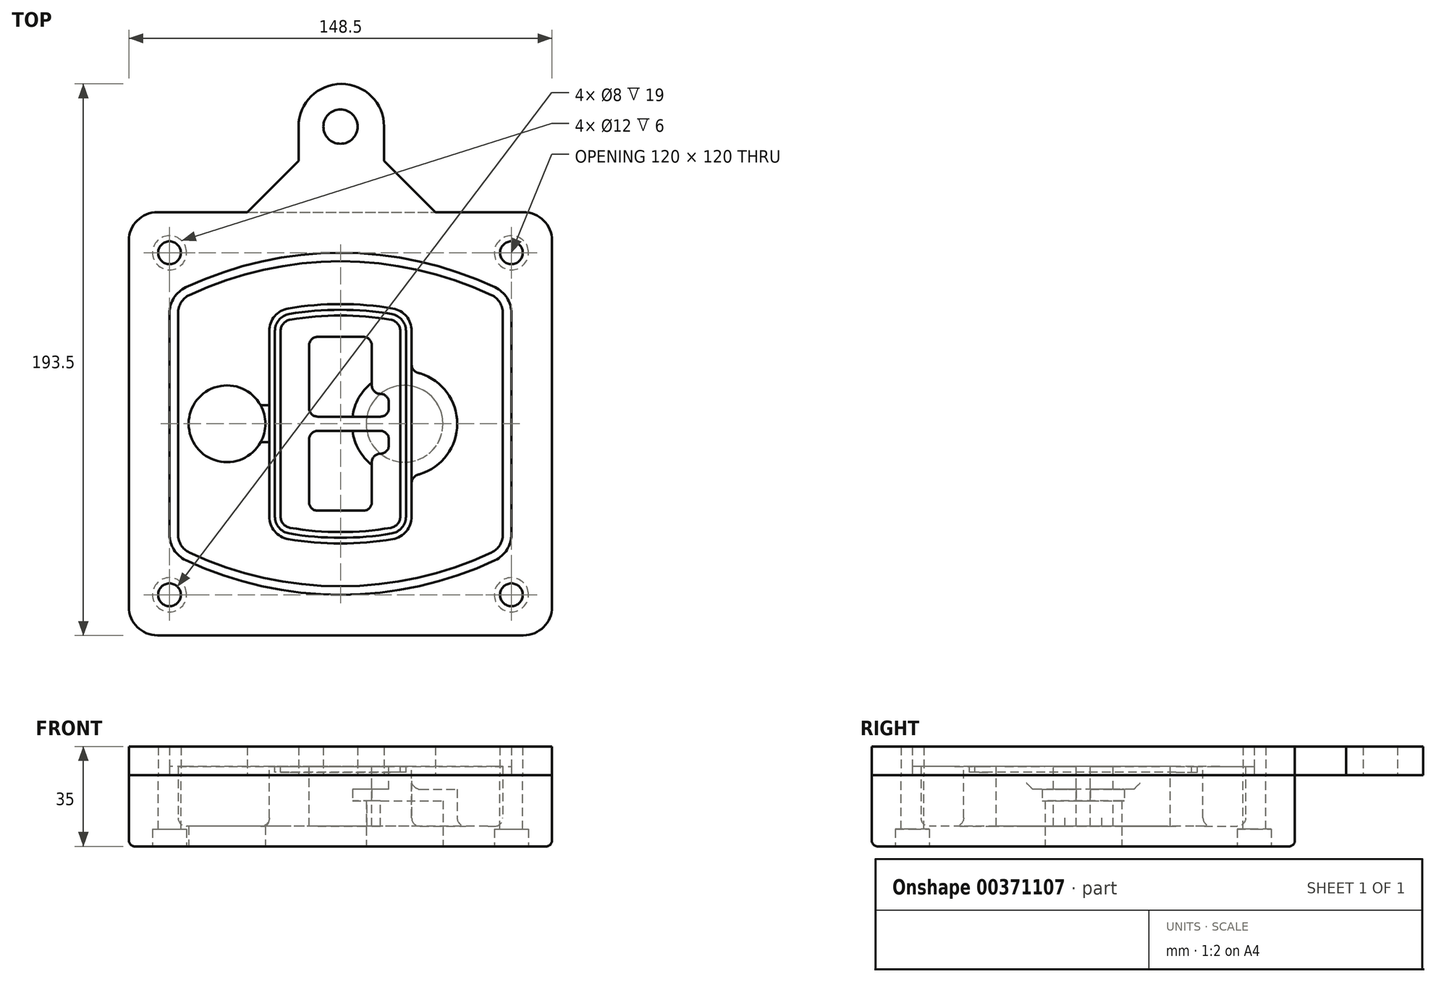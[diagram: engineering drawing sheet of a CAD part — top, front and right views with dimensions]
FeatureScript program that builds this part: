
annotation { "Feature Type Name" : "Feature", "Feature Type Description" : "" }
export const myFeature = defineFeature(function(context is Context, id is Id, definition is map)
    precondition{}
    {
        {
            var Q0;
            Q0=qCreatedBy(makeId("Top.planeOp"),FACE);
            var sketch = newSketch(context, id + "F0", { "sketchPlane" : qUnion([Q0])});
            skPoint(sketch, "E0.rect.middle", {"position": v(0, 0) * mm});
            skLineSegment(sketch, "E1.bottom", {"start": v(-64.25, -74.25) * mm, "end": v(64.25, -74.25) * mm});
            skLineSegment(sketch, "E1.top", {"start": v(-64.25, 74.25) * mm, "end": v(64.25, 74.25) * mm});
            skLineSegment(sketch, "E1.left", {"start": v(-74.25, -64.25) * mm, "end": v(-74.25, 64.25) * mm});
            skLineSegment(sketch, "E1.right", {"start": v(74.25, -64.25) * mm, "end": v(74.25, 64.25) * mm});
            skLineSegment(sketch, "E2", {"start": v(-74.25, 74.25) * mm, "end": v(74.25, -74.25) * mm, "construction": true});
            skLineSegment(sketch, "E3", {"start": v(74.25, 74.25) * mm, "end": v(-74.25, -74.25) * mm, "construction": true});
            skCircle(sketch, "E4", {"center": v(-60, 60) * mm, "radius": 4 * mm});
            skCircle(sketch, "E5", {"center": v(60, 60) * mm, "radius": 4 * mm});
            skCircle(sketch, "E6", {"center": v(60, -60) * mm, "radius": 4 * mm});
            skCircle(sketch, "E7", {"center": v(-60, -60) * mm, "radius": 4 * mm});
            skLineSegment(sketch, "E8", {"start": v(-60, 60) * mm, "end": v(60, 60) * mm, "construction": true});
            skLineSegment(sketch, "E9", {"start": v(60, 60) * mm, "end": v(60, -60) * mm, "construction": true});
            skLineSegment(sketch, "E10", {"start": v(60, -60) * mm, "end": v(-60, -60) * mm, "construction": true});
            skLineSegment(sketch, "E11", {"start": v(-60, -60) * mm, "end": v(-60, 60) * mm, "construction": true});
            skLineSegment(sketch, "E12", {"start": v(-60, 38.83) * mm, "end": v(-60, -38.83) * mm});
            skLineSegment(sketch, "E13", {"start": v(60, 38.83) * mm, "end": v(60, -38.83) * mm});
            skArc(sketch, "E14", {"start": v(54.26, 47.88) * mm, "mid": v(0, 60) * mm, "end": v(-54.26, 47.88) * mm});
            skArc(sketch, "E15", {"start": v(-54.26, -47.88) * mm, "mid": v(0, -60) * mm, "end": v(54.26, -47.88) * mm});
            skLineSegment(sketch, "E16", {"start": v(-60, 0) * mm, "end": v(60, 0) * mm, "construction": true});
            skPoint(sketch, "E17.visualSharp", {"position": v(-60, -45) * mm});
            skArc(sketch, "E17.filletArc", {"start": v(-60, -38.83) * mm, "mid": v(-58.44, -44.2) * mm, "end": v(-54.26, -47.88) * mm});
            skPoint(sketch, "E18.visualSharp", {"position": v(-60, 45) * mm});
            skArc(sketch, "E18.filletArc", {"start": v(-54.26, 47.88) * mm, "mid": v(-58.44, 44.2) * mm, "end": v(-60, 38.83) * mm});
            skPoint(sketch, "E19.visualSharp", {"position": v(60, 45) * mm});
            skArc(sketch, "E19.filletArc", {"start": v(60, 38.83) * mm, "mid": v(58.44, 44.2) * mm, "end": v(54.26, 47.88) * mm});
            skPoint(sketch, "E20.visualSharp", {"position": v(60, -45) * mm});
            skArc(sketch, "E20.filletArc", {"start": v(54.26, -47.88) * mm, "mid": v(58.44, -44.2) * mm, "end": v(60, -38.83) * mm});
            skPoint(sketch, "E21.visualSharp", {"position": v(-74.25, 74.25) * mm});
            skArc(sketch, "E21.filletArc", {"start": v(-64.25, 74.25) * mm, "mid": v(-71.32, 71.32) * mm, "end": v(-74.25, 64.25) * mm});
            skPoint(sketch, "E22.visualSharp", {"position": v(74.25, 74.25) * mm});
            skArc(sketch, "E22.filletArc", {"start": v(74.25, 64.25) * mm, "mid": v(71.32, 71.32) * mm, "end": v(64.25, 74.25) * mm});
            skPoint(sketch, "E23.visualSharp", {"position": v(74.25, -74.25) * mm});
            skArc(sketch, "E23.filletArc", {"start": v(64.25, -74.25) * mm, "mid": v(71.32, -71.32) * mm, "end": v(74.25, -64.25) * mm});
            skPoint(sketch, "E24.visualSharp", {"position": v(-74.25, -74.25) * mm});
            skArc(sketch, "E24.filletArc", {"start": v(-74.25, -64.25) * mm, "mid": v(-71.32, -71.32) * mm, "end": v(-64.25, -74.25) * mm});
            skArc(sketch, "E25.0", {"start": v(57, 38.83) * mm, "mid": v(55.9, 42.58) * mm, "end": v(52.98, 45.17) * mm});
            skLineSegment(sketch, "E25.1", {"start": v(57, 38.83) * mm, "end": v(57, -38.83) * mm});
            skArc(sketch, "E25.2", {"start": v(52.98, -45.17) * mm, "mid": v(55.9, -42.58) * mm, "end": v(57, -38.83) * mm});
            skArc(sketch, "E25.3", {"start": v(-52.98, -45.17) * mm, "mid": v(0, -57) * mm, "end": v(52.98, -45.17) * mm});
            skArc(sketch, "E25.4", {"start": v(-57, -38.83) * mm, "mid": v(-55.9, -42.58) * mm, "end": v(-52.98, -45.17) * mm});
            skArc(sketch, "E25.5", {"start": v(52.98, 45.17) * mm, "mid": v(0, 57) * mm, "end": v(-52.98, 45.17) * mm});
            skLineSegment(sketch, "E25.6", {"start": v(-57, 38.83) * mm, "end": v(-57, -38.83) * mm});
            skArc(sketch, "E25.7", {"start": v(-52.98, 45.17) * mm, "mid": v(-55.9, 42.58) * mm, "end": v(-57, 38.83) * mm});
            skArc(sketch, "E26.0", {"start": v(-55.96, 51.5) * mm, "mid": v(-61.82, 46.33) * mm, "end": v(-64, 38.83) * mm});
            skArc(sketch, "E26.1", {"start": v(55.96, 51.5) * mm, "mid": v(0, 64) * mm, "end": v(-55.96, 51.5) * mm});
            skArc(sketch, "E26.2", {"start": v(64, 38.83) * mm, "mid": v(61.82, 46.33) * mm, "end": v(55.96, 51.5) * mm});
            skLineSegment(sketch, "E26.3", {"start": v(64, 38.83) * mm, "end": v(64, -38.83) * mm});
            skArc(sketch, "E26.4", {"start": v(55.96, -51.5) * mm, "mid": v(61.82, -46.33) * mm, "end": v(64, -38.83) * mm});
            skLineSegment(sketch, "E26.5", {"start": v(-64, 38.83) * mm, "end": v(-64, -38.83) * mm});
            skArc(sketch, "E26.6", {"start": v(-55.96, -51.5) * mm, "mid": v(0, -64) * mm, "end": v(55.96, -51.5) * mm});
            skArc(sketch, "E26.7", {"start": v(-64, -38.83) * mm, "mid": v(-61.82, -46.33) * mm, "end": v(-55.96, -51.5) * mm});
            skSolve(sketch);
        }
        {
            var Q0;
            Q0=makeQuery(id+"F0.imprint","IMPRINT",FACE,{"disambiguationData":[TD([[makeQuery(id+"F0.imprint","IMPRINT",EDGE,{"derivedFrom":sQuery(id+"F0.wireOp",EDGE,"E1.bottom")}),1.0]])]});
            var Q1;
            Q1=makeQuery(id+"F0.imprint","IMPRINT",FACE,{"disambiguationData":[TD([[makeQuery(id+"F0.imprint","IMPRINT",EDGE,{"derivedFrom":sQuery(id+"F0.wireOp",EDGE,"E12")}),1.0]])]});
            var Q2;
            Q2=makeQuery(id+"F0.imprint","IMPRINT",FACE,{"disambiguationData":[TD([[makeQuery(id+"F0.imprint","IMPRINT",EDGE,{"derivedFrom":sQuery(id+"F0.wireOp",EDGE,"E25.0")}),1.0]])]});
            var Q3;
            Q3=makeQuery(id+"F0.imprint","IMPRINT",FACE,{"disambiguationData":[TD([[makeQuery(id+"F0.imprint","IMPRINT",EDGE,{"derivedFrom":sQuery(id+"F0.wireOp",EDGE,"E12")}),-1.0]])]});
            extrude(context, id + "F1", {"entities" : qUnion([Q0, Q1, Q2, Q3]), "oppositeDirection" : true, "depth" : 25 * mm});
        }
        {
            var Q0;
            Q0=makeQuery(id+"F0.imprint","IMPRINT",FACE,{"disambiguationData":[TD([[makeQuery(id+"F0.imprint","IMPRINT",EDGE,{"derivedFrom":sQuery(id+"F0.wireOp",EDGE,"E12")}),1.0]])]});
            extrude(context, id + "F2", {"entities" : qUnion([Q0]), "operationType" : NewBodyOperationType.ADD, "depth" : 3 * mm});
        }
        {
            var Q0;
            Q0=makeQuery(id+"F0.imprint","IMPRINT",FACE,{"disambiguationData":[TD([[makeQuery(id+"F0.imprint","IMPRINT",EDGE,{"derivedFrom":sQuery(id+"F0.wireOp",EDGE,"E25.0")}),1.0]])]});
            extrude(context, id + "F3", {"entities" : qUnion([Q0]), "operationType" : NewBodyOperationType.REMOVE, "oppositeDirection" : true, "depth" : 18 * mm});
        }
        {
            var Q0;
            Q0=makeQuery(id+"F2.opExtrude","CAP_FACE",FACE,{"disambiguationData":[OSD([sQuery(id+"F0.wireOp",EDGE,"E12"),sQuery(id+"F0.wireOp",EDGE,"E13"),sQuery(id+"F0.wireOp",EDGE,"E14"),sQuery(id+"F0.wireOp",EDGE,"E15"),sQuery(id+"F0.wireOp",EDGE,"E17.filletArc"),sQuery(id+"F0.wireOp",EDGE,"E18.filletArc"),sQuery(id+"F0.wireOp",EDGE,"E19.filletArc"),sQuery(id+"F0.wireOp",EDGE,"E20.filletArc"),sQuery(id+"F0.wireOp",EDGE,"E25.0"),sQuery(id+"F0.wireOp",EDGE,"E25.1"),sQuery(id+"F0.wireOp",EDGE,"E25.2"),sQuery(id+"F0.wireOp",EDGE,"E25.3"),sQuery(id+"F0.wireOp",EDGE,"E25.4"),sQuery(id+"F0.wireOp",EDGE,"E25.5"),sQuery(id+"F0.wireOp",EDGE,"E25.6"),sQuery(id+"F0.wireOp",EDGE,"E25.7")])],"isStart":false});
            var sketch = newSketch(context, id + "F4", { "sketchPlane" : qUnion([Q0])});
            skArc(sketch, "E27.0", {"start": v(-18.34, -40.45) * mm, "mid": v(0, -42) * mm, "end": v(18.34, -40.45) * mm});
            skArc(sketch, "E28.0", {"start": v(18.34, 40.45) * mm, "mid": v(0, 42) * mm, "end": v(-18.34, 40.45) * mm});
            skLineSegment(sketch, "E29", {"start": v(-25, 32.57) * mm, "end": v(-25, -32.57) * mm});
            skLineSegment(sketch, "E30", {"start": v(25, 32.57) * mm, "end": v(25, -32.57) * mm});
            skLineSegment(sketch, "E31", {"start": v(-25, 39.1) * mm, "end": v(25, 39.1) * mm, "construction": true});
            skLineSegment(sketch, "E32", {"start": v(-25, -39.1) * mm, "end": v(25, -39.1) * mm, "construction": true});
            skPoint(sketch, "E33.visualSharp", {"position": v(-25, 39.1) * mm});
            skArc(sketch, "E33.filletArc", {"start": v(-18.34, 40.45) * mm, "mid": v(-23.11, 37.73) * mm, "end": v(-25, 32.57) * mm});
            skPoint(sketch, "E34.visualSharp", {"position": v(25, 39.1) * mm});
            skArc(sketch, "E34.filletArc", {"start": v(25, 32.57) * mm, "mid": v(23.11, 37.73) * mm, "end": v(18.34, 40.45) * mm});
            skPoint(sketch, "E35.visualSharp", {"position": v(25, -39.1) * mm});
            skArc(sketch, "E35.filletArc", {"start": v(18.34, -40.45) * mm, "mid": v(23.11, -37.73) * mm, "end": v(25, -32.57) * mm});
            skPoint(sketch, "E36.visualSharp", {"position": v(-25, -39.1) * mm});
            skArc(sketch, "E36.filletArc", {"start": v(-25, -32.57) * mm, "mid": v(-23.11, -37.73) * mm, "end": v(-18.34, -40.45) * mm});
            skArc(sketch, "E37.0", {"start": v(52.98, 45.17) * mm, "mid": v(0, 57) * mm, "end": v(-52.98, 45.17) * mm});
            skArc(sketch, "E37.1", {"start": v(-52.98, 45.17) * mm, "mid": v(-55.9, 42.58) * mm, "end": v(-57, 38.83) * mm});
            skLineSegment(sketch, "E37.2", {"start": v(-57, 38.83) * mm, "end": v(-57, -38.83) * mm});
            skArc(sketch, "E37.3", {"start": v(-57, -38.83) * mm, "mid": v(-55.9, -42.58) * mm, "end": v(-52.98, -45.17) * mm});
            skArc(sketch, "E37.4", {"start": v(-52.98, -45.17) * mm, "mid": v(0, -57) * mm, "end": v(52.98, -45.17) * mm});
            skArc(sketch, "E37.5", {"start": v(52.98, -45.17) * mm, "mid": v(55.9, -42.58) * mm, "end": v(57, -38.83) * mm});
            skLineSegment(sketch, "E37.6", {"start": v(57, 38.83) * mm, "end": v(57, -38.83) * mm});
            skArc(sketch, "E37.7", {"start": v(57, 38.83) * mm, "mid": v(55.9, 42.58) * mm, "end": v(52.98, 45.17) * mm});
            skLineSegment(sketch, "E38.0", {"start": v(23, 32.57) * mm, "end": v(23, -32.57) * mm});
            skArc(sketch, "E38.1", {"start": v(18, -38.48) * mm, "mid": v(21.58, -36.44) * mm, "end": v(23, -32.57) * mm});
            skArc(sketch, "E38.2", {"start": v(-18, -38.48) * mm, "mid": v(0, -40) * mm, "end": v(18, -38.48) * mm});
            skArc(sketch, "E38.3", {"start": v(-23, -32.57) * mm, "mid": v(-21.58, -36.44) * mm, "end": v(-18, -38.48) * mm});
            skLineSegment(sketch, "E38.4", {"start": v(-23, 32.57) * mm, "end": v(-23, -32.57) * mm});
            skArc(sketch, "E38.5", {"start": v(23, 32.57) * mm, "mid": v(21.58, 36.44) * mm, "end": v(18, 38.48) * mm});
            skArc(sketch, "E38.6", {"start": v(-18, 38.48) * mm, "mid": v(-21.58, 36.44) * mm, "end": v(-23, 32.57) * mm});
            skArc(sketch, "E38.7", {"start": v(18, 38.48) * mm, "mid": v(0, 40) * mm, "end": v(-18, 38.48) * mm});
            skArc(sketch, "E39.0", {"start": v(21, 32.57) * mm, "mid": v(20.06, 35.15) * mm, "end": v(17.67, 36.5) * mm});
            skLineSegment(sketch, "E39.1", {"start": v(21, 32.57) * mm, "end": v(21, -32.57) * mm});
            skArc(sketch, "E39.2", {"start": v(17.67, -36.5) * mm, "mid": v(20.06, -35.15) * mm, "end": v(21, -32.57) * mm});
            skArc(sketch, "E39.3", {"start": v(-17.67, -36.5) * mm, "mid": v(0, -38) * mm, "end": v(17.67, -36.5) * mm});
            skArc(sketch, "E39.4", {"start": v(-21, -32.57) * mm, "mid": v(-20.06, -35.15) * mm, "end": v(-17.67, -36.5) * mm});
            skArc(sketch, "E39.5", {"start": v(17.67, 36.5) * mm, "mid": v(0, 38) * mm, "end": v(-17.67, 36.5) * mm});
            skLineSegment(sketch, "E39.6", {"start": v(-21, 32.57) * mm, "end": v(-21, -32.57) * mm});
            skArc(sketch, "E39.7", {"start": v(-17.67, 36.5) * mm, "mid": v(-20.06, 35.15) * mm, "end": v(-21, 32.57) * mm});
            skLineSegment(sketch, "E40", {"start": v(-25, 0) * mm, "end": v(25, 0) * mm, "construction": true});
            skLineSegment(sketch, "E41", {"start": v(-11, 5.5) * mm, "end": v(-11, 27.5) * mm});
            skLineSegment(sketch, "E42", {"start": v(-8, 30.5) * mm, "end": v(8, 30.5) * mm});
            skLineSegment(sketch, "E43", {"start": v(11, 27.5) * mm, "end": v(11, 13.5) * mm});
            skLineSegment(sketch, "E44", {"start": v(14, 10.5) * mm, "end": v(14, 10.5) * mm});
            skLineSegment(sketch, "E45", {"start": v(17, 7.5) * mm, "end": v(17, 5.5) * mm});
            skLineSegment(sketch, "E46", {"start": v(14, 2.5) * mm, "end": v(-8, 2.5) * mm});
            skPoint(sketch, "E47.visualSharp", {"position": v(-11, 30.5) * mm});
            skArc(sketch, "E47.filletArc", {"start": v(-8, 30.5) * mm, "mid": v(-10.12, 29.62) * mm, "end": v(-11, 27.5) * mm});
            skPoint(sketch, "E48.visualSharp", {"position": v(11, 30.5) * mm});
            skArc(sketch, "E48.filletArc", {"start": v(11, 27.5) * mm, "mid": v(10.12, 29.62) * mm, "end": v(8, 30.5) * mm});
            skPoint(sketch, "E49.visualSharp", {"position": v(11, 10.5) * mm});
            skArc(sketch, "E49.filletArc", {"start": v(11, 13.5) * mm, "mid": v(11.88, 11.38) * mm, "end": v(14, 10.5) * mm});
            skPoint(sketch, "E50.visualSharp", {"position": v(17, 10.5) * mm});
            skArc(sketch, "E50.filletArc", {"start": v(17, 7.5) * mm, "mid": v(16.12, 9.62) * mm, "end": v(14, 10.5) * mm});
            skPoint(sketch, "E51.visualSharp", {"position": v(17, 2.5) * mm});
            skArc(sketch, "E51.filletArc", {"start": v(14, 2.5) * mm, "mid": v(16.12, 3.38) * mm, "end": v(17, 5.5) * mm});
            skPoint(sketch, "E52.visualSharp", {"position": v(-11, 2.5) * mm});
            skArc(sketch, "E52.filletArc", {"start": v(-11, 5.5) * mm, "mid": v(-10.12, 3.38) * mm, "end": v(-8, 2.5) * mm});
            skLineSegment(sketch, "E53.0.MirrorCS", {"start": v(14, -2.5) * mm, "end": v(-8, -2.5) * mm});
            skArc(sketch, "E54.0.MirrorCS", {"start": v(-11, -5.5) * mm, "mid": v(-10.12, -3.38) * mm, "end": v(-8, -2.5) * mm});
            skLineSegment(sketch, "E55.0.MirrorCS", {"start": v(-11, -5.5) * mm, "end": v(-11, -27.5) * mm});
            skArc(sketch, "E56.0.MirrorCS", {"start": v(-8, -30.5) * mm, "mid": v(-10.12, -29.62) * mm, "end": v(-11, -27.5) * mm});
            skLineSegment(sketch, "E57.0.MirrorCS", {"start": v(-8, -30.5) * mm, "end": v(8, -30.5) * mm});
            skArc(sketch, "E58.0.MirrorCS", {"start": v(11, -27.5) * mm, "mid": v(10.12, -29.62) * mm, "end": v(8, -30.5) * mm});
            skLineSegment(sketch, "E59.0.MirrorCS", {"start": v(11, -27.5) * mm, "end": v(11, -13.5) * mm});
            skArc(sketch, "E60.0.MirrorCS", {"start": v(11, -13.5) * mm, "mid": v(11.88, -11.38) * mm, "end": v(14, -10.5) * mm});
            skArc(sketch, "E61.0.MirrorCS", {"start": v(17, -7.5) * mm, "mid": v(16.12, -9.62) * mm, "end": v(14, -10.5) * mm});
            skLineSegment(sketch, "E62.0.MirrorCS", {"start": v(17, -7.5) * mm, "end": v(17, -5.5) * mm});
            skArc(sketch, "E63.0.MirrorCS", {"start": v(14, -2.5) * mm, "mid": v(16.12, -3.38) * mm, "end": v(17, -5.5) * mm});
            skSolve(sketch);
        }
        {
            var Q0;
            Q0=makeQuery(id+"F4.imprint","IMPRINT",FACE,{"disambiguationData":[TD([[makeQuery(id+"F4.imprint","IMPRINT",EDGE,{"derivedFrom":sQuery(id+"F4.wireOp",EDGE,"E27.0")}),1.0]])]});
            var Q1;
            Q1=makeQuery(id+"F4.imprint","IMPRINT",FACE,{"disambiguationData":[TD([[makeQuery(id+"F4.imprint","IMPRINT",EDGE,{"derivedFrom":sQuery(id+"F4.wireOp",EDGE,"E38.0")}),-1.0]])]});
            var Q2;
            Q2=makeQuery(id+"F4.imprint","IMPRINT",FACE,{"disambiguationData":[TD([[makeQuery(id+"F4.imprint","IMPRINT",EDGE,{"derivedFrom":sQuery(id+"F4.wireOp",EDGE,"E39.0")}),1.0]])]});
            extrude(context, id + "F5", {"entities" : qUnion([Q0, Q1, Q2]), "operationType" : NewBodyOperationType.ADD, "endBound" : BoundingType.UP_TO_NEXT, "oppositeDirection" : true, "depth" : 25 * mm});
        }
        {
            var Q0;
            Q0=makeQuery(id+"F4.imprint","IMPRINT",FACE,{"disambiguationData":[TD([[makeQuery(id+"F4.imprint","IMPRINT",EDGE,{"derivedFrom":sQuery(id+"F4.wireOp",EDGE,"E38.0")}),-1.0]])]});
            extrude(context, id + "F6", {"entities" : qUnion([Q0]), "operationType" : NewBodyOperationType.REMOVE, "oppositeDirection" : true, "depth" : 2 * mm});
        }
        {
            var Q0;
            Q0=makeQuery(id+"F1.opExtrude","CAP_FACE",FACE,{"disambiguationData":[OSD([sQuery(id+"F0.wireOp",EDGE,"E1.bottom"),sQuery(id+"F0.wireOp",EDGE,"E1.top"),sQuery(id+"F0.wireOp",EDGE,"E1.left"),sQuery(id+"F0.wireOp",EDGE,"E1.right"),sQuery(id+"F0.wireOp",EDGE,"E4"),sQuery(id+"F0.wireOp",EDGE,"E5"),sQuery(id+"F0.wireOp",EDGE,"E6"),sQuery(id+"F0.wireOp",EDGE,"E7"),sQuery(id+"F0.wireOp",EDGE,"E21.filletArc"),sQuery(id+"F0.wireOp",EDGE,"E22.filletArc"),sQuery(id+"F0.wireOp",EDGE,"E23.filletArc"),sQuery(id+"F0.wireOp",EDGE,"E24.filletArc")])],"isStart":false});
            var sketch = newSketch(context, id + "F7", { "sketchPlane" : qUnion([Q0])});
            skCircle(sketch, "E64", {"center": v(22.5, 0) * mm, "radius": 13.47 * mm});
            skCircle(sketch, "E65", {"center": v(-39.81, 0) * mm, "radius": 13.47 * mm});
            skLineSegment(sketch, "E66", {"start": v(74.25, 0) * mm, "end": v(-74.25, 0) * mm});
            skCircle(sketch, "E67", {"center": v(22.5, 0) * mm, "radius": 18.47 * mm});
            skCircle(sketch, "E68", {"center": v(60, -60) * mm, "radius": 6 * mm});
            skCircle(sketch, "E69", {"center": v(-60, -60) * mm, "radius": 6 * mm});
            skCircle(sketch, "E70", {"center": v(-60, 60) * mm, "radius": 6 * mm});
            skCircle(sketch, "E71", {"center": v(60, 60) * mm, "radius": 6 * mm});
            skSolve(sketch);
        }
        {
            var Q0;
            {var subQ1=sQuery(id+"F7.wireOp",EDGE,"E66");var subQ4=sQuery(id+"F7.wireOp",EDGE,"E64");var subQ6=makeQuery(id+"F7.imprint","INTERSECT",VERTEX,{"disambiguationData":[OD(0.0)],"derivedFrom":[subQ4,subQ1]});Q0=makeQuery(id+"F7.imprint","IMPRINT",FACE,{"disambiguationData":[TD([[makeQuery(id+"F7.imprint","IMPRINT",EDGE,{"disambiguationData":[TD([[subQ6,-1.0]])],"derivedFrom":subQ4}),-1.0]])]});}
            var Q1;
            {var subQ0=sQuery(id+"F7.wireOp",EDGE,"E66");var subQ1=sQuery(id+"F7.wireOp",EDGE,"E64");var subQ3=makeQuery(id+"F7.imprint","INTERSECT",VERTEX,{"disambiguationData":[OD(0.0)],"derivedFrom":[subQ1,subQ0]});Q1=makeQuery(id+"F7.imprint","IMPRINT",FACE,{"disambiguationData":[TD([[makeQuery(id+"F7.imprint","IMPRINT",EDGE,{"disambiguationData":[TD([[subQ3,-1.0]])],"derivedFrom":subQ1}),1.0]])]});}
            var Q2;
            {var subQ0=sQuery(id+"F7.wireOp",EDGE,"E66");var subQ1=sQuery(id+"F7.wireOp",EDGE,"E64");var subQ3=makeQuery(id+"F7.imprint","INTERSECT",VERTEX,{"disambiguationData":[OD(0.0)],"derivedFrom":[subQ1,subQ0]});Q2=makeQuery(id+"F7.imprint","IMPRINT",FACE,{"disambiguationData":[TD([[makeQuery(id+"F7.imprint","IMPRINT",EDGE,{"disambiguationData":[TD([[subQ3,1.0]])],"derivedFrom":subQ1}),1.0]])]});}
            var Q3;
            {var subQ1=sQuery(id+"F7.wireOp",EDGE,"E66");var subQ4=sQuery(id+"F7.wireOp",EDGE,"E64");var subQ6=makeQuery(id+"F7.imprint","INTERSECT",VERTEX,{"disambiguationData":[OD(0.0)],"derivedFrom":[subQ4,subQ1]});Q3=makeQuery(id+"F7.imprint","IMPRINT",FACE,{"disambiguationData":[TD([[makeQuery(id+"F7.imprint","IMPRINT",EDGE,{"disambiguationData":[TD([[subQ6,1.0]])],"derivedFrom":subQ4}),-1.0]])]});}
            extrude(context, id + "F8", {"entities" : qUnion([Q0, Q1, Q2, Q3]), "operationType" : NewBodyOperationType.ADD, "oppositeDirection" : true, "depth" : 20 * mm});
        }
        {
            var Q0;
            {var subQ0=sQuery(id+"F7.wireOp",EDGE,"E66");var subQ1=sQuery(id+"F7.wireOp",EDGE,"E64");var subQ3=makeQuery(id+"F7.imprint","INTERSECT",VERTEX,{"disambiguationData":[OD(0.0)],"derivedFrom":[subQ1,subQ0]});Q0=makeQuery(id+"F7.imprint","IMPRINT",FACE,{"disambiguationData":[TD([[makeQuery(id+"F7.imprint","IMPRINT",EDGE,{"disambiguationData":[TD([[subQ3,-1.0]])],"derivedFrom":subQ1}),1.0]])]});}
            var Q1;
            {var subQ0=sQuery(id+"F7.wireOp",EDGE,"E66");var subQ1=sQuery(id+"F7.wireOp",EDGE,"E64");var subQ3=makeQuery(id+"F7.imprint","INTERSECT",VERTEX,{"disambiguationData":[OD(0.0)],"derivedFrom":[subQ1,subQ0]});Q1=makeQuery(id+"F7.imprint","IMPRINT",FACE,{"disambiguationData":[TD([[makeQuery(id+"F7.imprint","IMPRINT",EDGE,{"disambiguationData":[TD([[subQ3,1.0]])],"derivedFrom":subQ1}),1.0]])]});}
            extrude(context, id + "F9", {"entities" : qUnion([Q0, Q1]), "operationType" : NewBodyOperationType.REMOVE, "oppositeDirection" : true, "depth" : 16 * mm});
        }
        {
            var Q0;
            {var subQ0=sQuery(id+"F7.wireOp",EDGE,"E66");var subQ1=sQuery(id+"F7.wireOp",EDGE,"E65");var subQ3=makeQuery(id+"F7.imprint","INTERSECT",VERTEX,{"disambiguationData":[OD(0.0)],"derivedFrom":[subQ1,subQ0]});Q0=makeQuery(id+"F7.imprint","IMPRINT",FACE,{"disambiguationData":[TD([[makeQuery(id+"F7.imprint","IMPRINT",EDGE,{"disambiguationData":[TD([[subQ3,-1.0]])],"derivedFrom":subQ1}),1.0]])]});}
            var Q1;
            {var subQ0=sQuery(id+"F7.wireOp",EDGE,"E66");var subQ1=sQuery(id+"F7.wireOp",EDGE,"E65");var subQ3=makeQuery(id+"F7.imprint","INTERSECT",VERTEX,{"disambiguationData":[OD(0.0)],"derivedFrom":[subQ1,subQ0]});Q1=makeQuery(id+"F7.imprint","IMPRINT",FACE,{"disambiguationData":[TD([[makeQuery(id+"F7.imprint","IMPRINT",EDGE,{"disambiguationData":[TD([[subQ3,1.0]])],"derivedFrom":subQ1}),1.0]])]});}
            extrude(context, id + "F10", {"entities" : qUnion([Q0, Q1]), "operationType" : NewBodyOperationType.REMOVE, "oppositeDirection" : true, "depth" : 25 * mm});
        }
        {
            var Q0;
            Q0=makeQuery(id+"F7.imprint","IMPRINT",FACE,{"disambiguationData":[TD([[makeQuery(id+"F7.imprint","IMPRINT",EDGE,{"derivedFrom":sQuery(id+"F7.wireOp",EDGE,"E68")}),1.0]])]});
            var Q1;
            Q1=makeQuery(id+"F7.imprint","IMPRINT",FACE,{"disambiguationData":[TD([[makeQuery(id+"F7.imprint","IMPRINT",EDGE,{"derivedFrom":makeQuery(id+"F1.opExtrude","CAP_EDGE",EDGE,{"disambiguationData":[OSD([sQuery(id+"F0.wireOp",EDGE,"E5")])],"isStart":false})}),-1.0]])]});
            var Q2;
            Q2=makeQuery(id+"F7.imprint","IMPRINT",FACE,{"disambiguationData":[TD([[makeQuery(id+"F7.imprint","IMPRINT",EDGE,{"derivedFrom":sQuery(id+"F7.wireOp",EDGE,"E69")}),1.0]])]});
            var Q3;
            Q3=makeQuery(id+"F7.imprint","IMPRINT",FACE,{"disambiguationData":[TD([[makeQuery(id+"F7.imprint","IMPRINT",EDGE,{"derivedFrom":makeQuery(id+"F1.opExtrude","CAP_EDGE",EDGE,{"disambiguationData":[OSD([sQuery(id+"F0.wireOp",EDGE,"E4")])],"isStart":false})}),-1.0]])]});
            var Q4;
            Q4=makeQuery(id+"F7.imprint","IMPRINT",FACE,{"disambiguationData":[TD([[makeQuery(id+"F7.imprint","IMPRINT",EDGE,{"derivedFrom":sQuery(id+"F7.wireOp",EDGE,"E70")}),1.0]])]});
            var Q5;
            Q5=makeQuery(id+"F7.imprint","IMPRINT",FACE,{"disambiguationData":[TD([[makeQuery(id+"F7.imprint","IMPRINT",EDGE,{"derivedFrom":makeQuery(id+"F1.opExtrude","CAP_EDGE",EDGE,{"disambiguationData":[OSD([sQuery(id+"F0.wireOp",EDGE,"E7")])],"isStart":false})}),-1.0]])]});
            var Q6;
            Q6=makeQuery(id+"F7.imprint","IMPRINT",FACE,{"disambiguationData":[TD([[makeQuery(id+"F7.imprint","IMPRINT",EDGE,{"derivedFrom":sQuery(id+"F7.wireOp",EDGE,"E71")}),1.0]])]});
            var Q7;
            Q7=makeQuery(id+"F7.imprint","IMPRINT",FACE,{"disambiguationData":[TD([[makeQuery(id+"F7.imprint","IMPRINT",EDGE,{"derivedFrom":makeQuery(id+"F1.opExtrude","CAP_EDGE",EDGE,{"disambiguationData":[OSD([sQuery(id+"F0.wireOp",EDGE,"E6")])],"isStart":false})}),-1.0]])]});
            extrude(context, id + "F11", {"entities" : qUnion([Q0, Q1, Q2, Q3, Q4, Q5, Q6, Q7]), "operationType" : NewBodyOperationType.REMOVE, "oppositeDirection" : true, "depth" : 6 * mm});
        }
        {
            var Q0;
            Q0=makeQuery(id+"F9.boolean.opBoolean","COPY",FACE,{"derivedFrom":makeQuery(id+"F9.opExtrude","CAP_FACE",FACE,{"disambiguationData":[OSD([sQuery(id+"F7.wireOp",EDGE,"E64")])],"isStart":false})});
            var sketch = newSketch(context, id + "F12", { "sketchPlane" : qUnion([Q0])});
            skArc(sketch, "E72.0", {"start": v(11, 14.45) * mm, "mid": v(6.45, 9.13) * mm, "end": v(4.2, 2.5) * mm});
            skArc(sketch, "E72.1", {"start": v(4.2, -2.5) * mm, "mid": v(6.45, -9.13) * mm, "end": v(11, -14.45) * mm});
            skLineSegment(sketch, "E73", {"start": v(4.2, -2.5) * mm, "end": v(14, -2.5) * mm});
            skLineSegment(sketch, "E74.0", {"start": v(14, 2.5) * mm, "end": v(4.2, 2.5) * mm});
            skArc(sketch, "E74.1", {"start": v(14, 2.5) * mm, "mid": v(16.12, 3.38) * mm, "end": v(17, 5.5) * mm});
            skLineSegment(sketch, "E74.2", {"start": v(17, 7.5) * mm, "end": v(17, 5.5) * mm});
            skArc(sketch, "E74.3", {"start": v(17, 7.5) * mm, "mid": v(16.12, 9.62) * mm, "end": v(14, 10.5) * mm});
            skArc(sketch, "E74.4", {"start": v(11, 13.5) * mm, "mid": v(11.88, 11.38) * mm, "end": v(14, 10.5) * mm});
            skLineSegment(sketch, "E74.5", {"start": v(11, 14.45) * mm, "end": v(11, 13.5) * mm});
            skLineSegment(sketch, "E74.7", {"start": v(14, -2.5) * mm, "end": v(4.2, -2.5) * mm});
            skArc(sketch, "E74.8", {"start": v(14, -2.5) * mm, "mid": v(16.12, -3.38) * mm, "end": v(17, -5.5) * mm});
            skLineSegment(sketch, "E74.9", {"start": v(17, -7.5) * mm, "end": v(17, -5.5) * mm});
            skArc(sketch, "E74.10", {"start": v(17, -7.5) * mm, "mid": v(16.12, -9.62) * mm, "end": v(14, -10.5) * mm});
            skArc(sketch, "E74.11", {"start": v(11, -13.5) * mm, "mid": v(11.88, -11.38) * mm, "end": v(14, -10.5) * mm});
            skLineSegment(sketch, "E74.12", {"start": v(11, -14.45) * mm, "end": v(11, -13.5) * mm});
            skPoint(sketch, "E75.orphan", {"position": v(11, -27.5) * mm});
            skPoint(sketch, "E76.orphan", {"position": v(-8, -2.5) * mm});
            skPoint(sketch, "E77.orphan", {"position": v(-8, 2.5) * mm});
            skPoint(sketch, "E78.orphan", {"position": v(11, 27.5) * mm});
            skSolve(sketch);
        }
        {
            var Q0;
            {var subQ7=sQuery(id+"F12.wireOp",EDGE,"E72.0");var subQ14=sQuery(id+"F12.wireOp",EDGE,"E72.1");var subQ16=sQuery(id+"F12.wireOp",EDGE,"E74.1");var subQ18=sQuery(id+"F12.wireOp",EDGE,"E74.8");Q0=qUnion([makeQuery(id+"F12.imprint","IMPRINT",FACE,{"disambiguationData":[TD([[makeQuery(id+"F12.imprint","IMPRINT",EDGE,{"derivedFrom":subQ7}),1.0]])]}),makeQuery(id+"F12.imprint","IMPRINT",FACE,{"disambiguationData":[TD([[makeQuery(id+"F12.imprint","IMPRINT",EDGE,{"derivedFrom":subQ14}),1.0]])]}),makeQuery(id+"F12.imprint","IMPRINT",FACE,{"disambiguationData":[TD([[makeQuery(id+"F12.imprint","IMPRINT",EDGE,{"derivedFrom":subQ16}),1.0]])]}),makeQuery(id+"F12.imprint","IMPRINT",FACE,{"disambiguationData":[TD([[makeQuery(id+"F12.imprint","IMPRINT",EDGE,{"derivedFrom":subQ18}),-1.0]])]})]);}
            var Q1;
            Q1=makeQuery(id+"F5.boolean.opBoolean","SPLIT",FACE,{"disambiguationData":[TD([makeQuery(id+"F5.opExtrude","SWEPT_FACE",FACE,{"disambiguationData":[OSD([sQuery(id+"F4.wireOp",EDGE,"E41")])]})])],"derivedFrom":makeQuery(id+"F3.boolean.opBoolean","COPY",FACE,{"derivedFrom":makeQuery(id+"F3.opExtrude","CAP_FACE",FACE,{"disambiguationData":[OSD([sQuery(id+"F0.wireOp",EDGE,"E25.0"),sQuery(id+"F0.wireOp",EDGE,"E25.1"),sQuery(id+"F0.wireOp",EDGE,"E25.2"),sQuery(id+"F0.wireOp",EDGE,"E25.3"),sQuery(id+"F0.wireOp",EDGE,"E25.4"),sQuery(id+"F0.wireOp",EDGE,"E25.5"),sQuery(id+"F0.wireOp",EDGE,"E25.6"),sQuery(id+"F0.wireOp",EDGE,"E25.7")])],"isStart":false})})});
            extrude(context, id + "F13", {"entities" : qUnion([Q0]), "operationType" : NewBodyOperationType.REMOVE, "endBound" : BoundingType.UP_TO_SURFACE, "endBoundEntityFace" : qUnion([Q1]), "depth" : 25 * mm});
        }
        {
            var Q0;
            Q0=makeQuery(id+"F3.boolean.opBoolean","COPY",EDGE,{"derivedFrom":makeQuery(id+"F3.opExtrude","CAP_EDGE",EDGE,{"disambiguationData":[OSD([sQuery(id+"F0.wireOp",EDGE,"E25.6")])],"isStart":false})});
            var Q1;
            Q1=makeQuery(id+"F8.boolean.opBoolean","INTERSECT",EDGE,{"derivedFrom":[makeQuery(id+"F5.opExtrude","SWEPT_FACE",FACE,{"disambiguationData":[OSD([sQuery(id+"F4.wireOp",EDGE,"E30")])]}),makeQuery(id+"F8.opExtrude","CAP_FACE",FACE,{"disambiguationData":[OSD([sQuery(id+"F7.wireOp",EDGE,"E67")])],"isStart":false})]});
            var Q2;
            Q2=makeQuery(id+"F8.boolean.opBoolean","INTERSECT",EDGE,{"disambiguationData":[OD(1.0)],"derivedFrom":[makeQuery(id+"F5.opExtrude","SWEPT_FACE",FACE,{"disambiguationData":[OSD([sQuery(id+"F4.wireOp",EDGE,"E30")])]}),makeQuery(id+"F8.opExtrude","SWEPT_FACE",FACE,{"disambiguationData":[OSD([sQuery(id+"F7.wireOp",EDGE,"E67")])]})]});
            var Q3;
            {var subQ0=sQuery(id+"F4.wireOp",EDGE,"E30");Q3=makeQuery(id+"F8.boolean.opBoolean","SPLIT",EDGE,{"disambiguationData":[TD([makeQuery(id+"F5.opExtrude","SWEPT_FACE",FACE,{"disambiguationData":[OSD([sQuery(id+"F4.wireOp",EDGE,"E35.filletArc")])]})])],"derivedFrom":makeQuery(id+"F5.opExtrude","CAP_EDGE",EDGE,{"disambiguationData":[OSD([subQ0])],"isStart":false})});}
            var Q4;
            {var subQ0=sQuery(id+"F0.wireOp",EDGE,"E25.7");var subQ1=sQuery(id+"F0.wireOp",EDGE,"E25.1");var subQ2=sQuery(id+"F0.wireOp",EDGE,"E25.6");var subQ3=sQuery(id+"F0.wireOp",EDGE,"E25.5");var subQ4=sQuery(id+"F0.wireOp",EDGE,"E25.4");var subQ5=sQuery(id+"F0.wireOp",EDGE,"E25.0");var subQ6=sQuery(id+"F0.wireOp",EDGE,"E25.2");var subQ7=sQuery(id+"F0.wireOp",EDGE,"E25.3");Q4=makeQuery(id+"F8.boolean.opBoolean","INTERSECT",EDGE,{"derivedFrom":[makeQuery(id+"F5.boolean.opBoolean","SPLIT",FACE,{"disambiguationData":[TD([makeQuery(id+"F2.opExtrude","SWEPT_FACE",FACE,{"disambiguationData":[OSD([subQ5])]})])],"derivedFrom":makeQuery(id+"F3.boolean.opBoolean","COPY",FACE,{"derivedFrom":makeQuery(id+"F3.opExtrude","CAP_FACE",FACE,{"disambiguationData":[OSD([subQ5,subQ1,subQ6,subQ7,subQ4,subQ3,subQ2,subQ0])],"isStart":false})})}),makeQuery(id+"F8.opExtrude","SWEPT_FACE",FACE,{"disambiguationData":[OSD([sQuery(id+"F7.wireOp",EDGE,"E67")])]})]});}
            var Q5;
            Q5=makeQuery(id+"F8.boolean.opBoolean","INTERSECT",EDGE,{"disambiguationData":[OD(0.0)],"derivedFrom":[makeQuery(id+"F5.opExtrude","SWEPT_FACE",FACE,{"disambiguationData":[OSD([sQuery(id+"F4.wireOp",EDGE,"E30")])]}),makeQuery(id+"F8.opExtrude","SWEPT_FACE",FACE,{"disambiguationData":[OSD([sQuery(id+"F7.wireOp",EDGE,"E67")])]})]});
            fillet(context, id + "F14", {"entities" : qUnion([Q0, Q1, Q2, Q3, Q4, Q5]), "radius" : 3 * mm, "tangentPropagation" : true, "allowEdgeOverflow" : false});
        }
        {
            var Q0;
            Q0=makeQuery(id+"F1.opExtrude","CAP_EDGE",EDGE,{"disambiguationData":[OSD([sQuery(id+"F0.wireOp",EDGE,"E1.bottom")])],"isStart":false});
            fillet(context, id + "F15", {"entities" : qUnion([Q0]), "radius" : 2 * mm, "tangentPropagation" : true, "allowEdgeOverflow" : false});
        }
        {
            var Q0;
            {var subQ0=sQuery(id+"F0.wireOp",EDGE,"E21.filletArc");var subQ1=sQuery(id+"F0.wireOp",EDGE,"E7");var subQ2=sQuery(id+"F0.wireOp",EDGE,"E6");var subQ3=sQuery(id+"F0.wireOp",EDGE,"E5");var subQ4=sQuery(id+"F0.wireOp",EDGE,"E4");var subQ5=sQuery(id+"F0.wireOp",EDGE,"E22.filletArc");var subQ6=sQuery(id+"F0.wireOp",EDGE,"E1.bottom");var subQ7=sQuery(id+"F0.wireOp",EDGE,"E1.right");var subQ8=sQuery(id+"F0.wireOp",EDGE,"E1.top");var subQ9=sQuery(id+"F0.wireOp",EDGE,"E1.left");var subQ10=sQuery(id+"F0.wireOp",EDGE,"E23.filletArc");var subQ11=sQuery(id+"F0.wireOp",EDGE,"E24.filletArc");Q0=makeQuery(id+"F2.boolean.opBoolean","SPLIT",FACE,{"disambiguationData":[TD([makeQuery(id+"F1.opExtrude","SWEPT_FACE",FACE,{"disambiguationData":[OSD([subQ6])]})])],"derivedFrom":makeQuery(id+"F1.opExtrude","CAP_FACE",FACE,{"disambiguationData":[OSD([subQ6,subQ8,subQ9,subQ7,subQ4,subQ3,subQ2,subQ1,subQ0,subQ5,subQ10,subQ11])],"isStart":true})});}
            var sketch = newSketch(context, id + "F16", { "sketchPlane" : qUnion([Q0])});
            skPoint(sketch, "E79.endSnap0", {"position": v(0, 74.25) * mm});
            skCircle(sketch, "E80", {"center": v(0, 104.25) * mm, "radius": 6 * mm});
            skLineSegment(sketch, "E81", {"start": v(-32.7, 74.25) * mm, "end": v(-14.7, 92.25) * mm});
            skLineSegment(sketch, "E82", {"start": v(15.3, 92.25) * mm, "end": v(33.3, 74.25) * mm});
            skLineSegment(sketch, "E83", {"start": v(-14.7, 92.25) * mm, "end": v(-14.7, 104.25) * mm});
            skLineSegment(sketch, "E84", {"start": v(15.3, 92.25) * mm, "end": v(15.3, 104.25) * mm});
            skArc(sketch, "E85", {"start": v(15.3, 104.25) * mm, "mid": v(0.3, 119.25) * mm, "end": v(-14.7, 104.25) * mm});
            skPoint(sketch, "E86.startSnap0", {"position": v(-74.25, 0) * mm});
            skPoint(sketch, "E86.endSnap0", {"position": v(74.25, 0) * mm});
            skPoint(sketch, "E87.MirrorP", {"position": v(0, -74.25) * mm});
            skArc(sketch, "E88.MirrorCS", {"start": v(15.3, -104.25) * mm, "mid": v(0.3, -119.25) * mm, "end": v(-14.7, -104.25) * mm});
            skLineSegment(sketch, "E89.MirrorCS", {"start": v(15.3, -92.25) * mm, "end": v(15.3, -104.25) * mm});
            skLineSegment(sketch, "E90.MirrorCS", {"start": v(15.3, -92.25) * mm, "end": v(33.3, -74.25) * mm});
            skCircle(sketch, "E91.MirrorC", {"center": v(0, -104.25) * mm, "radius": 6 * mm});
            skLineSegment(sketch, "E92.MirrorCS", {"start": v(-32.7, -74.25) * mm, "end": v(-14.7, -92.25) * mm});
            skLineSegment(sketch, "E93.MirrorCS", {"start": v(-14.7, -92.25) * mm, "end": v(-14.7, -104.25) * mm});
            skSolve(sketch);
        }
        {
            var Q0;
            Q0=makeQuery(id+"F16.imprint","IMPRINT",FACE,{"disambiguationData":[TD([[makeQuery(id+"F16.imprint","IMPRINT",EDGE,{"derivedFrom":sQuery(id+"F16.wireOp",EDGE,"E80")}),-1.0]])]});
            var Q1;
            Q1=makeQuery(id+"F16.imprint","IMPRINT",FACE,{"disambiguationData":[TD([[makeQuery(id+"F16.imprint","IMPRINT",EDGE,{"derivedFrom":makeQuery(id+"F1.opExtrude","CAP_EDGE",EDGE,{"disambiguationData":[OSD([sQuery(id+"F0.wireOp",EDGE,"E1.left")])],"isStart":true})}),-1.0]])]});
            var Q2;
            Q2=makeQuery(id+"F16.imprint","IMPRINT",FACE,{"disambiguationData":[TD([[makeQuery(id+"F16.imprint","IMPRINT",EDGE,{"derivedFrom":sQuery(id+"F16.wireOp",EDGE,"E88.MirrorCS")}),-1.0]])]});
            extrude(context, id + "F17", {"entities" : qUnion([Q0, Q1, Q2]), "depth" : 10 * mm});
        }
    });
